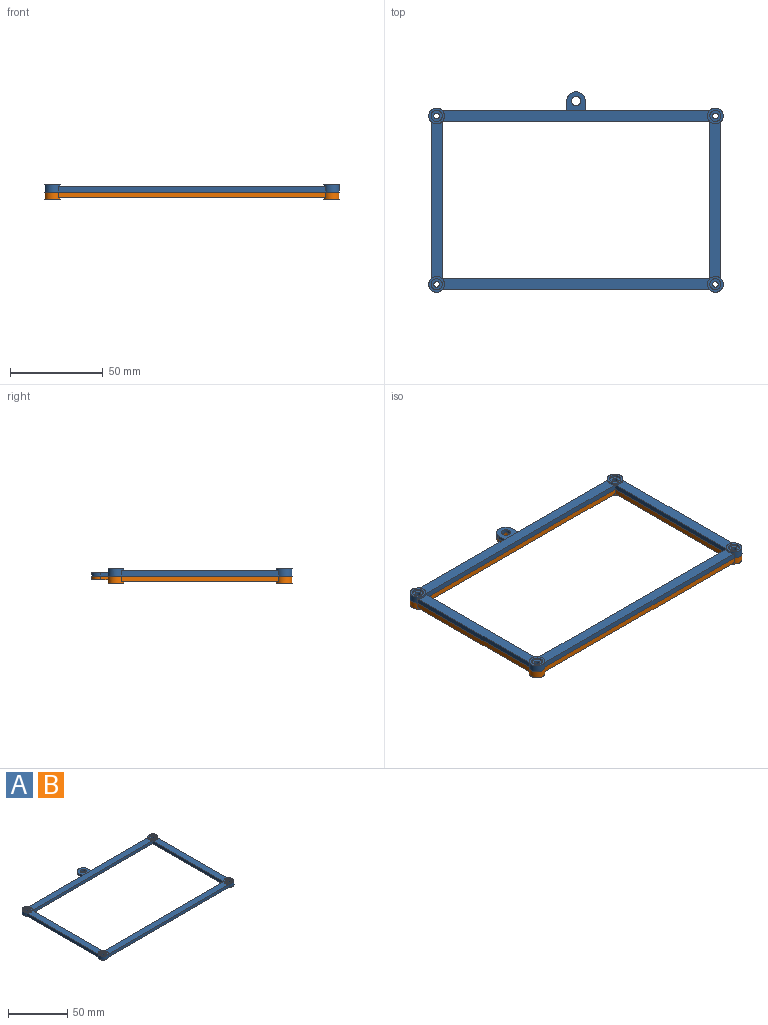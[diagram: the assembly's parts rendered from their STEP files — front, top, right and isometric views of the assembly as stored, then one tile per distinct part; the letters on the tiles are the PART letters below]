
ASSEMBLY  parts=2 mates=1
PART A: 38 faces, bbox 158.5x107.8x4 mm
  f0: cylinder r=4.24mm len=8.49mm, axis (0,0,-1), area 66.6mm2, adj f2,f3,f6,f8,f20,f22
  f1: cylinder r=3mm len=6mm, axis (0,0,-1), area 18.8mm2, adj f2,f5
  f2: plane 8.49x8.49mm, normal (0,0,1), area 28.3mm2, adj f0,f1
  f3: plane 158.49x107.84mm, normal (0,0,-1), area 2969.5mm2, adj f0,f4,f6,f7,f9,f11,f12,f14
  f4: cylinder r=1.5mm len=3mm, axis (0,0,-1), area 28.3mm2, adj f3,f5
  f5: plane 6x6mm, normal (0,0,1), area 21.2mm2, adj f1,f4
  f6: plane 144x3mm, normal (0,1,0), area 412mm2, adj f0,f3,f8,f30,f33,f34,f37
  f7: plane 144x3mm, normal (0,-1,0), area 432mm2, adj f3,f8,f12,f21
  f8: plane 144x6mm, normal (0,0,1), area 853.7mm2, adj f0,f6,f7,f30
  f9: cylinder r=1.5mm len=3mm, axis (0,0,-1), area 28.3mm2, adj f3,f10
  f10: plane 6x6mm, normal (0,0,1), area 21.2mm2, adj f9,f31
  f11: plane 84.6x3mm, normal (1,0,0), area 253.8mm2, adj f3,f13,f14,f30
  f12: plane 84.6x3mm, normal (-1,0,0), area 253.8mm2, adj f3,f7,f13,f17
  f13: plane 84.6x6mm, normal (0,0,1), area 497.3mm2, adj f11,f12,f14,f30
  f14: cylinder r=4.24mm len=8.49mm, axis (0,0,-1), area 66.6mm2, adj f3,f11,f13,f16,f18,f19
  f15: cylinder r=3mm len=6mm, axis (0,0,-1), area 18.8mm2, adj f16,f29
  f16: plane 8.49x8.49mm, normal (0,0,1), area 28.3mm2, adj f14,f15
  f17: plane 144x3mm, normal (0,1,0), area 432mm2, adj f3,f12,f19,f21
  f18: plane 144x3mm, normal (0,-1,0), area 432mm2, adj f3,f14,f19,f24
  f19: plane 144x6mm, normal (0,0,1), area 853.7mm2, adj f14,f17,f18,f24
  f20: plane 84.6x3mm, normal (-1,0,0), area 253.8mm2, adj f0,f3,f22,f24
  f21: plane 84.6x3mm, normal (1,0,0), area 253.8mm2, adj f3,f7,f17,f22
  f22: plane 84.6x6mm, normal (0,0,1), area 497.3mm2, adj f0,f20,f21,f24
  f23: cylinder r=3mm len=6mm, axis (0,0,-1), area 18.8mm2, adj f25,f27
  f24: cylinder r=4.24mm len=8.49mm, axis (0,0,-1), area 66.6mm2, adj f3,f18,f19,f20,f22,f25
  f25: plane 8.49x8.49mm, normal (0,0,1), area 28.3mm2, adj f23,f24
  f26: cylinder r=1.5mm len=3mm, axis (0,0,-1), area 28.3mm2, adj f3,f27
  f27: plane 6x6mm, normal (0,0,1), area 21.2mm2, adj f23,f26
  f28: cylinder r=1.5mm len=3mm, axis (0,0,-1), area 28.3mm2, adj f3,f29
  f29: plane 6x6mm, normal (0,0,1), area 21.2mm2, adj f15,f28
  f30: cylinder r=4.24mm len=8.49mm, axis (0,0,-1), area 66.6mm2, adj f3,f6,f8,f11,f13,f32
  f31: cylinder r=3mm len=6mm, axis (0,0,-1), area 18.8mm2, adj f10,f32
  f32: plane 8.49x8.49mm, normal (0,0,1), area 28.3mm2, adj f30,f31
  f33: plane 5.39x2mm, normal (-1,0,0), area 10.8mm2, adj f3,f6,f35,f37
  f34: plane 5.24x2mm, normal (1,0,0), area 10.5mm2, adj f3,f6,f35,f37
  f35: cylinder r=5mm len=9.98mm, axis (0,0,-1), area 30.2mm2, adj f3,f33,f34,f37
  f36: cylinder r=2.5mm len=5mm, axis (0,0,-1), area 31.4mm2, adj f3,f37
  f37: plane 10x9.98mm, normal (0,0,1), area 69.5mm2, adj f6,f33,f34,f35,f36
PART B: same geometry as A
PLACE A at identity
PLACE B rot(axis=(0,1,0),180deg) t=(-150,0,0)mm
MATE fastened B.f9 <-> A.f0  axis (0,0,1) through (-150,90.6,0)mm
